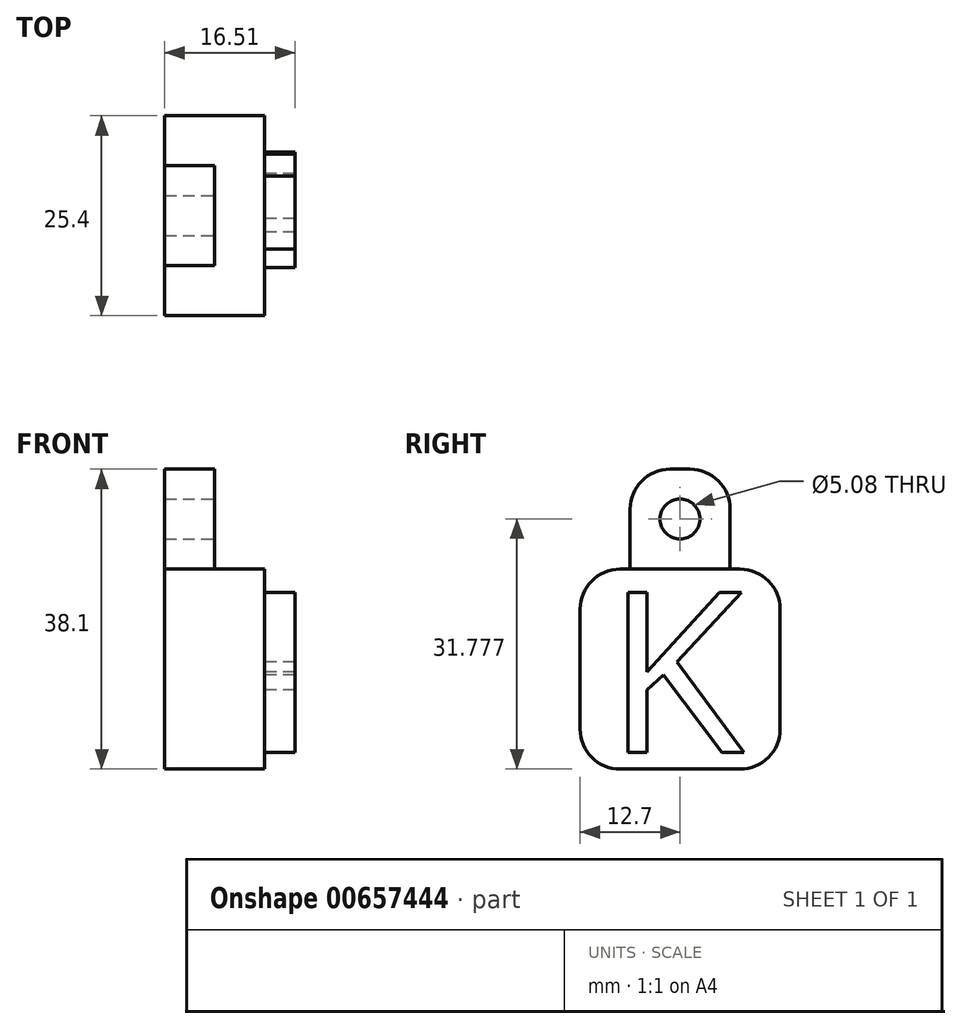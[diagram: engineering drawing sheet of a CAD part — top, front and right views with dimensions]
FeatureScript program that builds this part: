
annotation { "Feature Type Name" : "Feature", "Feature Type Description" : "" }
export const myFeature = defineFeature(function(context is Context, id is Id, definition is map)
    precondition{}
    {
        {
            var Q0;
            Q0=qCreatedBy(makeId("Right.planeOp"),FACE);
            var sketch = newSketch(context, id + "F0", { "sketchPlane" : qUnion([Q0])});
            skLineSegment(sketch, "E0.bottom", {"start": v(12.7, 12.7) * mm, "end": v(-12.7, 12.7) * mm});
            skLineSegment(sketch, "E0.top", {"start": v(12.7, -12.7) * mm, "end": v(-12.7, -12.7) * mm});
            skLineSegment(sketch, "E0.left", {"start": v(12.7, 12.7) * mm, "end": v(12.7, -12.7) * mm});
            skLineSegment(sketch, "E0.right", {"start": v(-12.7, 12.7) * mm, "end": v(-12.7, -12.7) * mm});
            skPoint(sketch, "E0.middle", {"position": v(0, 0) * mm});
            skSolve(sketch);
        }
        {
            var Q0;
            Q0 = qSketchRegion(id + "F0", true);
            extrude(context, id + "F1", {"entities" : qUnion([Q0]), "depth" : 12.7 * mm, "offsetDistance" : 25.4 * mm});
        }
        {
            var Q0;
            Q0=qCreatedBy(makeId("Right.planeOp"),FACE);
            var sketch = newSketch(context, id + "F2", { "sketchPlane" : qUnion([Q0])});
            skLineSegment(sketch, "E1.bottom", {"start": v(-6.35, 25.4) * mm, "end": v(6.35, 25.4) * mm});
            skLineSegment(sketch, "E1.top", {"start": v(-6.35, 12.7) * mm, "end": v(6.35, 12.7) * mm});
            skLineSegment(sketch, "E1.left", {"start": v(-6.35, 25.4) * mm, "end": v(-6.35, 12.7) * mm});
            skLineSegment(sketch, "E1.right", {"start": v(6.35, 25.4) * mm, "end": v(6.35, 12.7) * mm});
            skPoint(sketch, "E1.middle", {"position": v(0, 19.05) * mm});
            skSolve(sketch);
        }
        {
            var Q0;
            Q0=makeQuery(id+"F2.imprint","IMPRINT",FACE,{"disambiguationData":[TD([[makeQuery(id+"F2.imprint","IMPRINT",EDGE,{"derivedFrom":sQuery(id+"F2.wireOp",EDGE,"E1.bottom")}),-1.0]])]});
            extrude(context, id + "F3", {"entities" : qUnion([Q0]), "depth" : 6.35 * mm, "offsetDistance" : 25.4 * mm});
        }
        {
            var Q0;
            Q0=makeQuery(id+"F3.opExtrude","SWEPT_EDGE",EDGE,{"disambiguationData":[OSD([sQuery(id+"F2.wireOp",EDGE,"E1.bottom"),sQuery(id+"F2.wireOp",EDGE,"E1.right")])]});
            fillet(context, id + "F4", {"entities" : qUnion([Q0]), "radius" : 5.08 * mm, "tangentPropagation" : true, "allowEdgeOverflow" : false});
        }
        {
            var Q0;
            Q0=makeQuery(id+"F3.opExtrude","SWEPT_EDGE",EDGE,{"disambiguationData":[OSD([sQuery(id+"F2.wireOp",EDGE,"E1.bottom"),sQuery(id+"F2.wireOp",EDGE,"E1.left")])]});
            fillet(context, id + "F5", {"entities" : qUnion([Q0]), "radius" : 5.08 * mm, "tangentPropagation" : true, "allowEdgeOverflow" : false});
        }
        {
            var Q0;
            Q0=makeQuery(id+"F3.opExtrude","CAP_FACE",FACE,{"disambiguationData":[OSD([sQuery(id+"F2.wireOp",EDGE,"E1.bottom"),sQuery(id+"F2.wireOp",EDGE,"E1.top"),sQuery(id+"F2.wireOp",EDGE,"E1.left"),sQuery(id+"F2.wireOp",EDGE,"E1.right")])],"isStart":false});
            var sketch = newSketch(context, id + "F6", { "sketchPlane" : qUnion([Q0])});
            skCircle(sketch, "E2", {"center": v(0, 19.08) * mm, "radius": 2.54 * mm});
            skSolve(sketch);
        }
        {
            var Q0;
            Q0=sQuery(id+"F6.wireOp",VERTEX,"E2.center");
            var Q1;
            Q1=makeQuery(id+"F3.opExtrude","SWEPT_BODY",BODY,{"disambiguationData":[OSD([sQuery(id+"F2.wireOp",EDGE,"E1.bottom"),sQuery(id+"F2.wireOp",EDGE,"E1.top"),sQuery(id+"F2.wireOp",EDGE,"E1.left"),sQuery(id+"F2.wireOp",EDGE,"E1.right")])]});
            hole(context, id + "F7", {"style" : HoleStyle.SIMPLE, "endStyle" : HoleEndStyle.THROUGH, "holeDiameter" : 5.08 * mm, "majorDiameter" : 6.35 * mm, "isTappedThrough" : true, "tappedDepth" : 12.7 * mm, "tapClearance" : 3, "locations" : qUnion([Q0]), "scope" : qUnion([Q1])});
        }
        {
            var Q0;
            Q0=makeQuery(id+"F1.opExtrude","SWEPT_EDGE",EDGE,{"disambiguationData":[OSD([sQuery(id+"F0.wireOp",EDGE,"E0.bottom"),sQuery(id+"F0.wireOp",EDGE,"E0.right")])]});
            var Q1;
            Q1=makeQuery(id+"F1.opExtrude","SWEPT_EDGE",EDGE,{"disambiguationData":[OSD([sQuery(id+"F0.wireOp",EDGE,"E0.top"),sQuery(id+"F0.wireOp",EDGE,"E0.right")])]});
            var Q2;
            Q2=makeQuery(id+"F1.opExtrude","SWEPT_EDGE",EDGE,{"disambiguationData":[OSD([sQuery(id+"F0.wireOp",EDGE,"E0.top"),sQuery(id+"F0.wireOp",EDGE,"E0.left")])]});
            var Q3;
            Q3=makeQuery(id+"F1.opExtrude","SWEPT_EDGE",EDGE,{"disambiguationData":[OSD([sQuery(id+"F0.wireOp",EDGE,"E0.bottom"),sQuery(id+"F0.wireOp",EDGE,"E0.left")])]});
            fillet(context, id + "F8", {"entities" : qUnion([Q0, Q1, Q2, Q3]), "radius" : 5.08 * mm, "tangentPropagation" : true, "allowEdgeOverflow" : false});
        }
        {
            var Q0;
            Q0=makeQuery(id+"F1.opExtrude","CAP_FACE",FACE,{"disambiguationData":[OSD([sQuery(id+"F0.wireOp",EDGE,"E0.bottom"),sQuery(id+"F0.wireOp",EDGE,"E0.top"),sQuery(id+"F0.wireOp",EDGE,"E0.left"),sQuery(id+"F0.wireOp",EDGE,"E0.right")])],"isStart":false});
            var sketch = newSketch(context, id + "F9", { "sketchPlane" : qUnion([Q0])});
            skSolve(sketch);
        }
        {
            var Q0;
            {var subQ3=sQuery(id+"F0.wireOp",EDGE,"E0.bottom");Q0=makeQuery(id+"F9.imprint","IMPRINT",FACE,{"disambiguationData":[TD([[makeQuery(id+"F9.imprint","IMPRINT",EDGE,{"derivedFrom":makeQuery(id+"F1.opExtrude","CAP_EDGE",EDGE,{"disambiguationData":[OSD([subQ3])],"isStart":false})}),1.0]])]});}
            var sketch = newSketch(context, id + "F10", { "sketchPlane" : qUnion([Q0])});
            skText(sketch, "E3", { "text": "K", "fontName": "OpenSans-Regular.ttf"});
            const initialGuessF10  = {"E3": [-0.0094, -0.0106, 1, 0, 0.02055]};
            skSetInitialGuess(sketch, initialGuessF10);
            skSolve(sketch);
        }
        {
            var Q0;
            Q0 = qSketchRegion(id + "F10", true);
            extrude(context, id + "F11", {"entities" : qUnion([Q0]), "operationType" : NewBodyOperationType.ADD, "depth" : 3.8 * mm, "offsetDistance" : 25.4 * mm});
        }
    });
